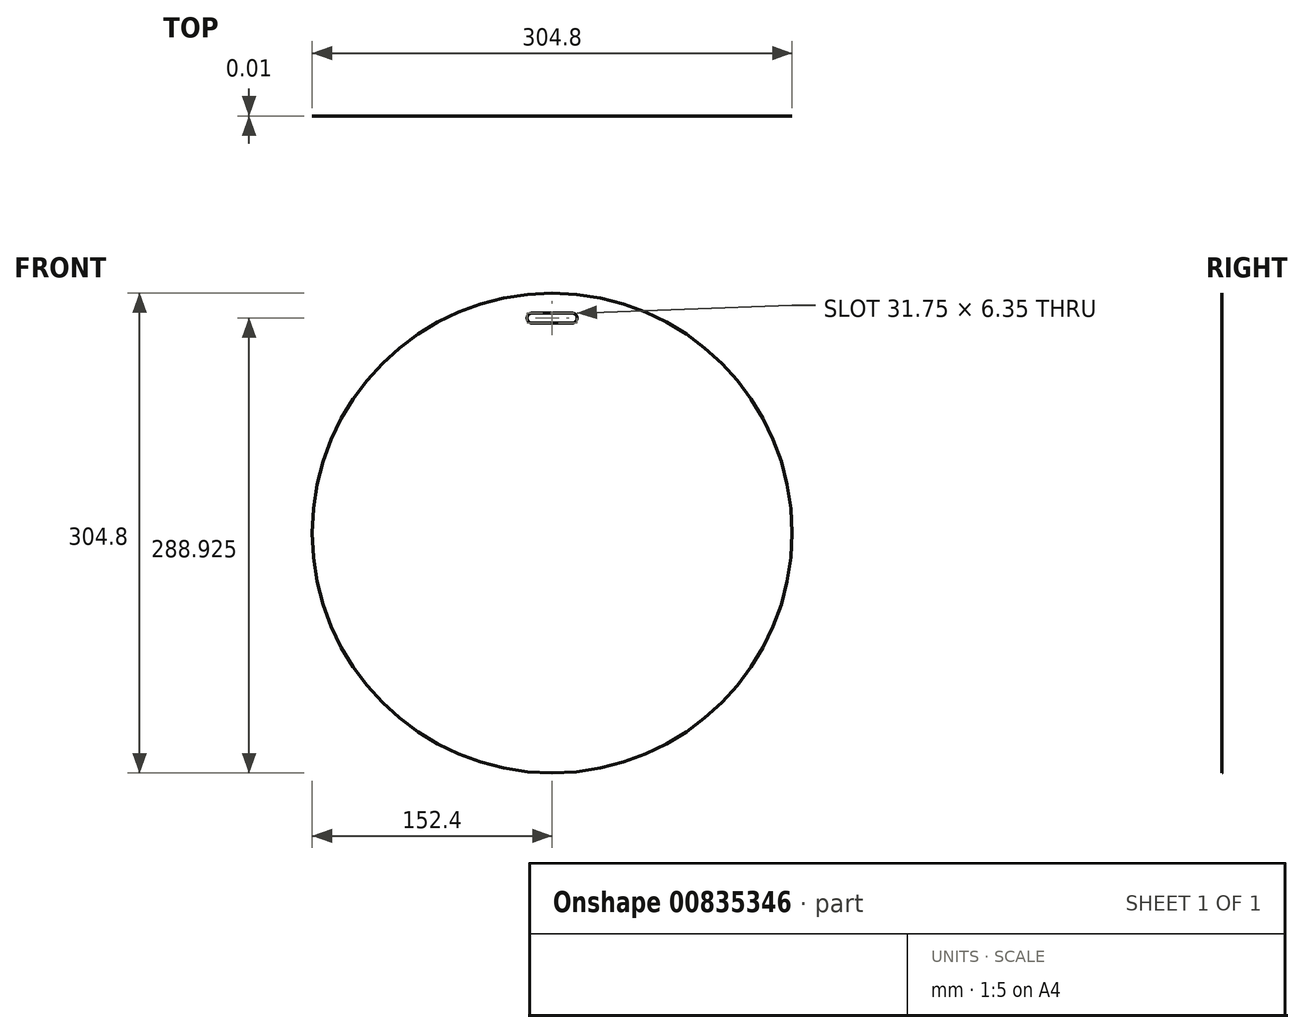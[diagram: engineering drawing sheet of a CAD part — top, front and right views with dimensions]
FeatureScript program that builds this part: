
annotation { "Feature Type Name" : "Feature", "Feature Type Description" : "" }
export const myFeature = defineFeature(function(context is Context, id is Id, definition is map)
    precondition{}
    {
        {
            var Q0;
            Q0=qCreatedBy(makeId("Front.planeOp"),FACE);
            var sketch = newSketch(context, id + "F0", { "sketchPlane" : qUnion([Q0])});
            skCircle(sketch, "E0", {"center": v(0, 0) * mm, "radius": 152.4 * mm});
            skLineSegment(sketch, "E1", {"start": v(0, 0) * mm, "end": v(0, 152.4) * mm});
            skLineSegment(sketch, "E2", {"start": v(-12.7, 136.53) * mm, "end": v(12.7, 136.53) * mm, "construction": true});
            skCircle(sketch, "E3", {"center": v(-12.7, 136.53) * mm, "radius": 3.18 * mm});
            skCircle(sketch, "E4", {"center": v(12.7, 136.53) * mm, "radius": 3.18 * mm});
            skLineSegment(sketch, "E5", {"start": v(-12.7, 139.7) * mm, "end": v(12.7, 139.7) * mm});
            skLineSegment(sketch, "E6", {"start": v(-12.7, 133.35) * mm, "end": v(12.7, 133.35) * mm});
            skSolve(sketch);
        }
        {
            var Q0;
            Q0=makeQuery(id+"F0.imprint","IMPRINT",FACE,{"disambiguationData":[TD([[makeQuery(id+"F0.imprint","IMPRINT",EDGE,{"derivedFrom":sQuery(id+"F0.wireOp",EDGE,"E0")}),1.0]])]});
            extrude(context, id + "F1", {"entities" : qUnion([Q0]), "depth" : 3 / 203.2 * mm, "offsetDistance" : 25.4 * mm});
        }
    });
